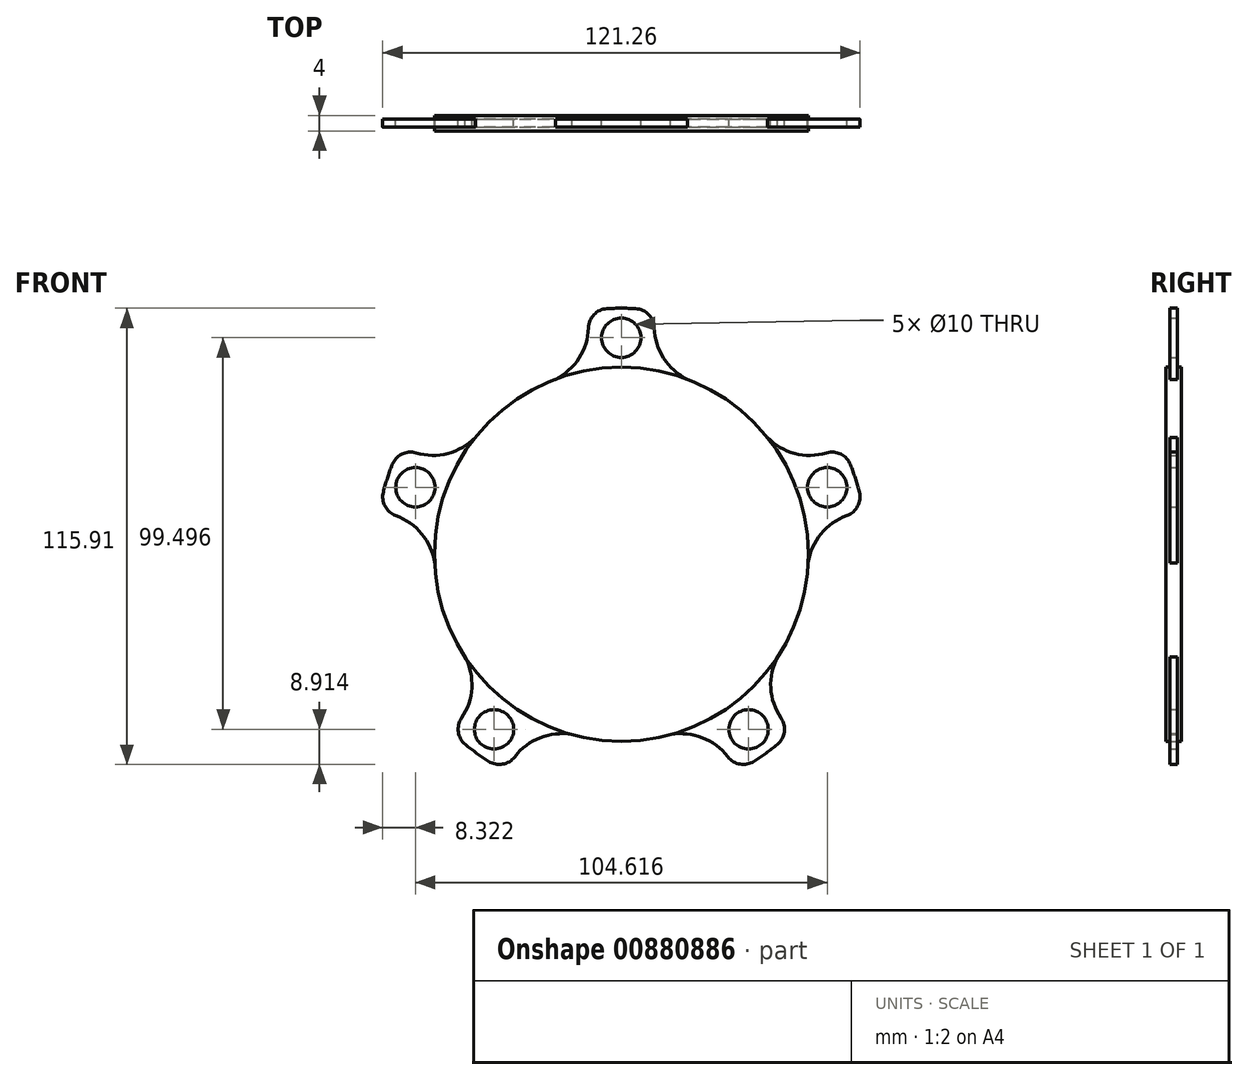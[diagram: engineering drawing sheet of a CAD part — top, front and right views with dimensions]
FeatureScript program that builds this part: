
annotation { "Feature Type Name" : "Feature", "Feature Type Description" : "" }
export const myFeature = defineFeature(function(context is Context, id is Id, definition is map)
    precondition{}
    {
        {
            var Q0;
            Q0=qCreatedBy(makeId("Front.planeOp"),FACE);
            var sketch = newSketch(context, id + "F0", { "sketchPlane" : qUnion([Q0])});
            skCircle(sketch, "E0", {"center": v(0, 0) * mm, "radius": 55 * mm, "construction": true});
            skCircle(sketch, "E1", {"center": v(0, 55) * mm, "radius": 5 * mm});
            skCircle(sketch, "E2.1.0", {"center": v(-52.3, 17) * mm, "radius": 5 * mm});
            skCircle(sketch, "E2.2.0", {"center": v(-32.33, -44.5) * mm, "radius": 5 * mm});
            skCircle(sketch, "E2.3.0", {"center": v(32.33, -44.5) * mm, "radius": 5 * mm});
            skCircle(sketch, "E2.4.0", {"center": v(52.3, 17) * mm, "radius": 5 * mm});
            skArc(sketch, "E3", {"start": v(-58.21, 22.75) * mm, "mid": v(-59.44, 19.31) * mm, "end": v(-60.47, 15.8) * mm});
            skArc(sketch, "E4", {"start": v(-52.14, 25.73) * mm, "mid": v(-44.06, 25.61) * mm, "end": v(-37.08, 29.68) * mm});
            skArc(sketch, "E5.MirrorCS", {"start": v(-57.3, 9.83) * mm, "mid": v(-50.7, 5.18) * mm, "end": v(-47.45, -2.22) * mm});
            skArc(sketch, "E6.1.0", {"start": v(-40.58, -41.64) * mm, "mid": v(-37.97, -34) * mm, "end": v(-39.7, -26.1) * mm});
            skArc(sketch, "E6.1.1", {"start": v(-27.06, -51.46) * mm, "mid": v(-20.6, -46.62) * mm, "end": v(-12.55, -45.81) * mm});
            skArc(sketch, "E6.2.0", {"start": v(27.06, -51.46) * mm, "mid": v(20.6, -46.62) * mm, "end": v(12.55, -45.81) * mm});
            skArc(sketch, "E6.2.1", {"start": v(40.58, -41.64) * mm, "mid": v(37.97, -34) * mm, "end": v(39.7, -26.1) * mm});
            skArc(sketch, "E6.3.0", {"start": v(57.3, 9.83) * mm, "mid": v(50.7, 5.18) * mm, "end": v(47.45, -2.22) * mm});
            skArc(sketch, "E6.3.1", {"start": v(52.14, 25.73) * mm, "mid": v(44.06, 25.61) * mm, "end": v(37.08, 29.68) * mm});
            skArc(sketch, "E6.4.0", {"start": v(8.36, 57.54) * mm, "mid": v(10.74, 49.82) * mm, "end": v(16.77, 44.44) * mm});
            skArc(sketch, "E6.4.1", {"start": v(-8.36, 57.54) * mm, "mid": v(-10.74, 49.82) * mm, "end": v(-16.77, 44.44) * mm});
            skArc(sketch, "E7.trimOffspring", {"start": v(3.65, 62.4) * mm, "mid": v(0, 62.5) * mm, "end": v(-3.65, 62.4) * mm});
            skArc(sketch, "E8.trimOffspring", {"start": v(60.47, 15.8) * mm, "mid": v(59.44, 19.31) * mm, "end": v(58.21, 22.75) * mm});
            skArc(sketch, "E9.trimOffspring", {"start": v(33.72, -52.62) * mm, "mid": v(36.74, -50.56) * mm, "end": v(39.63, -48.33) * mm});
            skArc(sketch, "E10.trimOffspring", {"start": v(-39.63, -48.33) * mm, "mid": v(-36.74, -50.56) * mm, "end": v(-33.72, -52.62) * mm});
            skPoint(sketch, "E11.visualSharp", {"position": v(-56.1, 27.55) * mm});
            skArc(sketch, "E11.filletArc", {"start": v(-52.14, 25.73) * mm, "mid": v(-55.76, 25.42) * mm, "end": v(-58.21, 22.75) * mm});
            skPoint(sketch, "E12.visualSharp", {"position": v(-61.58, 10.69) * mm});
            skArc(sketch, "E12.filletArc", {"start": v(-60.47, 15.8) * mm, "mid": v(-60.05, 12.2) * mm, "end": v(-57.3, 9.83) * mm});
            skPoint(sketch, "E13.visualSharp", {"position": v(-43.54, -44.84) * mm});
            skArc(sketch, "E13.filletArc", {"start": v(-40.58, -41.64) * mm, "mid": v(-41.4, -45.17) * mm, "end": v(-39.63, -48.33) * mm});
            skPoint(sketch, "E14.visualSharp", {"position": v(-29.2, -55.26) * mm});
            skArc(sketch, "E14.filletArc", {"start": v(-33.72, -52.62) * mm, "mid": v(-30.16, -53.34) * mm, "end": v(-27.06, -51.46) * mm});
            skPoint(sketch, "E15.visualSharp", {"position": v(43.54, -44.84) * mm});
            skArc(sketch, "E15.filletArc", {"start": v(39.63, -48.33) * mm, "mid": v(41.4, -45.17) * mm, "end": v(40.58, -41.64) * mm});
            skPoint(sketch, "E16.visualSharp", {"position": v(29.2, -55.26) * mm});
            skArc(sketch, "E16.filletArc", {"start": v(27.06, -51.46) * mm, "mid": v(30.16, -53.34) * mm, "end": v(33.72, -52.62) * mm});
            skPoint(sketch, "E17.visualSharp", {"position": v(61.58, 10.69) * mm});
            skArc(sketch, "E17.filletArc", {"start": v(57.3, 9.83) * mm, "mid": v(60.05, 12.2) * mm, "end": v(60.47, 15.8) * mm});
            skPoint(sketch, "E18.visualSharp", {"position": v(56.1, 27.55) * mm});
            skArc(sketch, "E18.filletArc", {"start": v(58.21, 22.75) * mm, "mid": v(55.76, 25.42) * mm, "end": v(52.14, 25.73) * mm});
            skPoint(sketch, "E19.visualSharp", {"position": v(-8.87, 61.87) * mm});
            skArc(sketch, "E19.filletArc", {"start": v(-3.65, 62.4) * mm, "mid": v(-6.95, 60.88) * mm, "end": v(-8.36, 57.54) * mm});
            skPoint(sketch, "E20.visualSharp", {"position": v(8.87, 61.87) * mm});
            skArc(sketch, "E20.filletArc", {"start": v(8.36, 57.54) * mm, "mid": v(6.95, 60.88) * mm, "end": v(3.65, 62.4) * mm});
            skArc(sketch, "E21", {"start": v(-16.77, 44.44) * mm, "mid": v(-27.92, 38.43) * mm, "end": v(-37.08, 29.68) * mm});
            skArc(sketch, "E22", {"start": v(16.77, 44.44) * mm, "mid": v(0, 47.5) * mm, "end": v(-16.77, 44.44) * mm});
            skLineSegment(sketch, "E23", {"start": v(37.08, 29.68) * mm, "end": v(37.08, 29.68) * mm});
            skArc(sketch, "E24", {"start": v(47.45, -2.22) * mm, "mid": v(39.7, 26.1) * mm, "end": v(16.77, 44.44) * mm});
            skArc(sketch, "E25", {"start": v(39.7, -26.1) * mm, "mid": v(45.18, -14.68) * mm, "end": v(47.45, -2.22) * mm});
            skArc(sketch, "E26", {"start": v(12.55, -45.81) * mm, "mid": v(27.92, -38.43) * mm, "end": v(39.7, -26.1) * mm});
            skArc(sketch, "E27", {"start": v(-12.55, -45.81) * mm, "mid": v(0, -47.5) * mm, "end": v(12.55, -45.81) * mm});
            skArc(sketch, "E28", {"start": v(-39.7, -26.1) * mm, "mid": v(-27.92, -38.43) * mm, "end": v(-12.55, -45.81) * mm});
            skLineSegment(sketch, "E29", {"start": v(-47.45, -2.22) * mm, "end": v(-47.45, -2.22) * mm});
            skArc(sketch, "E30", {"start": v(-37.08, 29.68) * mm, "mid": v(-45.18, 14.68) * mm, "end": v(-47.45, -2.22) * mm});
            skArc(sketch, "E31", {"start": v(-47.45, -2.22) * mm, "mid": v(-45.18, -14.68) * mm, "end": v(-39.7, -26.1) * mm});
            skSolve(sketch);
        }
        {
            var Q0;
            Q0=makeQuery(id+"F0.imprint","IMPRINT",FACE,{"disambiguationData":[TD([[makeQuery(id+"F0.imprint","IMPRINT",EDGE,{"derivedFrom":sQuery(id+"F0.wireOp",EDGE,"E21")}),1.0]])]});
            extrude(context, id + "F1", {"entities" : qUnion([Q0]), "endBound" : BoundingType.SYMMETRIC, "depth" : 4 * mm, "offsetDistance" : 25 * mm});
        }
        {
            var Q0;
            Q0=makeQuery(id+"F0.imprint","IMPRINT",FACE,{"disambiguationData":[TD([[makeQuery(id+"F0.imprint","IMPRINT",EDGE,{"derivedFrom":sQuery(id+"F0.wireOp",EDGE,"E2.1.0")}),-1.0]])]});
            var Q1;
            Q1=makeQuery(id+"F0.imprint","IMPRINT",FACE,{"disambiguationData":[TD([[makeQuery(id+"F0.imprint","IMPRINT",EDGE,{"derivedFrom":sQuery(id+"F0.wireOp",EDGE,"E1")}),-1.0]])]});
            var Q2;
            Q2=makeQuery(id+"F0.imprint","IMPRINT",FACE,{"disambiguationData":[TD([[makeQuery(id+"F0.imprint","IMPRINT",EDGE,{"derivedFrom":sQuery(id+"F0.wireOp",EDGE,"E2.4.0")}),-1.0]])]});
            var Q3;
            Q3=makeQuery(id+"F0.imprint","IMPRINT",FACE,{"disambiguationData":[TD([[makeQuery(id+"F0.imprint","IMPRINT",EDGE,{"derivedFrom":sQuery(id+"F0.wireOp",EDGE,"E2.3.0")}),-1.0]])]});
            var Q4;
            Q4=makeQuery(id+"F0.imprint","IMPRINT",FACE,{"disambiguationData":[TD([[makeQuery(id+"F0.imprint","IMPRINT",EDGE,{"derivedFrom":sQuery(id+"F0.wireOp",EDGE,"E2.2.0")}),-1.0]])]});
            extrude(context, id + "F2", {"entities" : qUnion([Q0, Q1, Q2, Q3, Q4]), "operationType" : NewBodyOperationType.ADD, "endBound" : BoundingType.SYMMETRIC, "depth" : 2 * mm, "offsetDistance" : 25 * mm});
        }
    });
